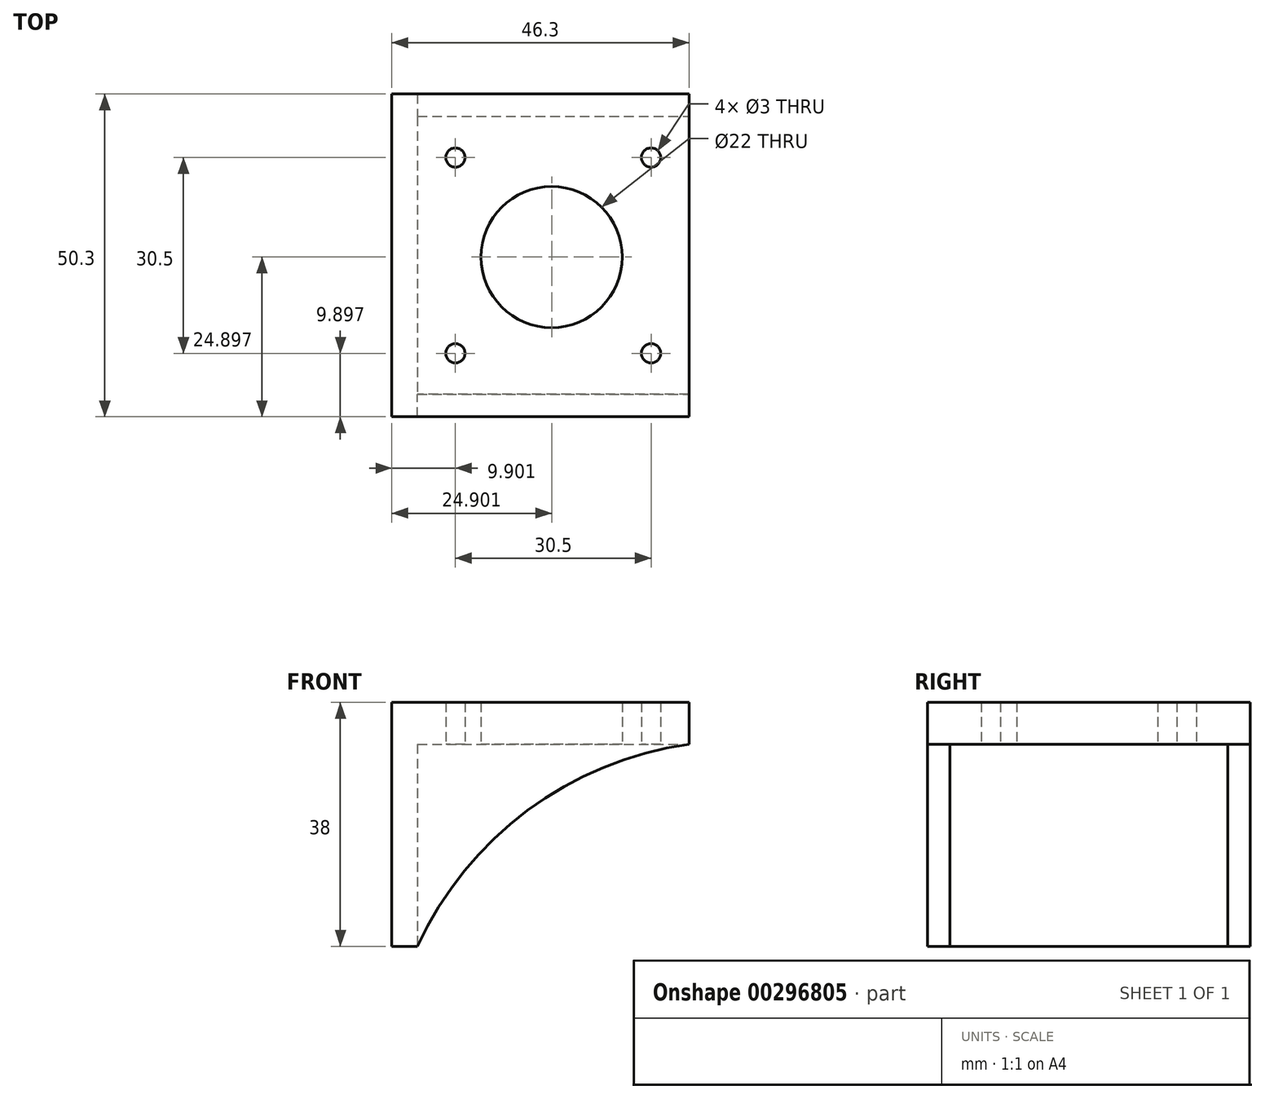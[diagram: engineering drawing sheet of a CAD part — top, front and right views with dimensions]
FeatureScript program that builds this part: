
annotation { "Feature Type Name" : "Feature", "Feature Type Description" : "" }
export const myFeature = defineFeature(function(context is Context, id is Id, definition is map)
    precondition{}
    {
        {
            var Q0;
            Q0=qCreatedBy(makeId("Top.planeOp"),FACE);
            var sketch = newSketch(context, id + "F0", { "sketchPlane" : qUnion([Q0])});
            skLineSegment(sketch, "E0.bottom", {"start": v(-20.2, 20.3) * mm, "end": v(22.1, 20.3) * mm});
            skLineSegment(sketch, "E0.top", {"start": v(-20.2, -22) * mm, "end": v(22.1, -22) * mm});
            skLineSegment(sketch, "E0.left", {"start": v(-20.2, 20.3) * mm, "end": v(-20.2, -22) * mm});
            skLineSegment(sketch, "E0.right", {"start": v(22.1, 20.3) * mm, "end": v(22.1, -22) * mm});
            skPoint(sketch, "E1", {"position": v(-14.3, 14.4) * mm});
            skPoint(sketch, "E2.0.1.0", {"position": v(-14.3, -16.1) * mm});
            skPoint(sketch, "E2.1.0.0", {"position": v(16.2, 14.4) * mm});
            skPoint(sketch, "E2.1.1.0", {"position": v(16.2, -16.1) * mm});
            skLineSegment(sketch, "E2.direction1", {"start": v(-14.3, 14.4) * mm, "end": v(16.2, 14.4) * mm, "construction": true});
            skLineSegment(sketch, "E2.direction2", {"start": v(-14.3, 14.4) * mm, "end": v(-14.3, -16.1) * mm, "construction": true});
            skCircle(sketch, "E3", {"center": v(-14.3, 14.4) * mm, "radius": 1.5 * mm});
            skCircle(sketch, "E4", {"center": v(16.2, 14.4) * mm, "radius": 1.5 * mm});
            skCircle(sketch, "E5", {"center": v(16.2, -16.1) * mm, "radius": 1.5 * mm});
            skCircle(sketch, "E6", {"center": v(-14.3, -16.1) * mm, "radius": 1.5 * mm});
            skCircle(sketch, "E7", {"center": v(0.7, -1.1) * mm, "radius": 2.5 * mm});
            skCircle(sketch, "E8", {"center": v(0.7, -1.1) * mm, "radius": 3.5 * mm, "construction": true});
            skCircle(sketch, "E9", {"center": v(0.7, -1.1) * mm, "radius": 11 * mm});
            skSolve(sketch);
        }
        {
            var Q0;
            Q0=makeQuery(id+"F0.imprint","IMPRINT",FACE,{"disambiguationData":[TD([[makeQuery(id+"F0.imprint","IMPRINT",EDGE,{"derivedFrom":sQuery(id+"F0.wireOp",EDGE,"E0.bottom")}),-1.0]])]});
            extrude(context, id + "F1", {"entities" : qUnion([Q0]), "depth" : 6.5 * mm});
        }
        {
            var Q0;
            Q0=makeQuery(id+"F1.opExtrude","SWEPT_FACE",FACE,{"disambiguationData":[OSD([sQuery(id+"F0.wireOp",EDGE,"E0.left")])]});
            var sketch = newSketch(context, id + "F2", { "sketchPlane" : qUnion([Q0])});
            skLineSegment(sketch, "E10.bottom", {"start": v(-20.3, 6.5) * mm, "end": v(22, 6.5) * mm});
            skLineSegment(sketch, "E10.top", {"start": v(-20.3, -31.5) * mm, "end": v(22, -31.5) * mm});
            skLineSegment(sketch, "E10.left", {"start": v(-20.3, 6.5) * mm, "end": v(-20.3, -31.5) * mm});
            skLineSegment(sketch, "E10.right", {"start": v(22, 6.5) * mm, "end": v(22, -31.5) * mm});
            skSolve(sketch);
        }
        {
            var Q0;
            Q0=qSketchRegion(id+"F2",true);
            extrude(context, id + "F3", {"entities" : qUnion([Q0]), "operationType" : NewBodyOperationType.ADD, "depth" : 4 * mm});
        }
        {
            var Q0;
            Q0=makeQuery(id+"F3.boolean.opBoolean","MERGE",FACE,{"derivedFrom":[makeQuery(id+"F1.opExtrude","SWEPT_FACE",FACE,{"disambiguationData":[OSD([sQuery(id+"F0.wireOp",EDGE,"E0.top")])]}),makeQuery(id+"F3.opExtrude","SWEPT_FACE",FACE,{"disambiguationData":[OSD([sQuery(id+"F2.wireOp",EDGE,"E10.right")])]})]});
            var sketch = newSketch(context, id + "F4", { "sketchPlane" : qUnion([Q0])});
            skArc(sketch, "E11", {"start": v(22.1, 0) * mm, "mid": v(-3.08, -10.35) * mm, "end": v(-20.2, -31.5) * mm});
            skSolve(sketch);
        }
        {
            var Q0;
            Q0=makeQuery(id+"F3.boolean.opBoolean","MERGE",FACE,{"derivedFrom":[makeQuery(id+"F1.opExtrude","SWEPT_FACE",FACE,{"disambiguationData":[OSD([sQuery(id+"F0.wireOp",EDGE,"E0.bottom")])]}),makeQuery(id+"F3.opExtrude","SWEPT_FACE",FACE,{"disambiguationData":[OSD([sQuery(id+"F2.wireOp",EDGE,"E10.left")])]})]});
            var sketch = newSketch(context, id + "F5", { "sketchPlane" : qUnion([Q0])});
            skArc(sketch, "E12", {"start": v(20.2, -31.5) * mm, "mid": v(3.08, -10.35) * mm, "end": v(-22.1, 0) * mm});
            skSolve(sketch);
        }
        {
            var Q0;
            Q0=makeQuery(id+"F5.imprint","IMPRINT",FACE,{"disambiguationData":[TD([[makeQuery(id+"F5.imprint","IMPRINT",EDGE,{"derivedFrom":sQuery(id+"F5.wireOp",EDGE,"E12")}),-1.0]])]});
            var Q1;
            {var subQ1=sQuery(id+"F0.wireOp",EDGE,"E0.bottom");Q1=makeQuery(id+"F5.imprint","IMPRINT",FACE,{"disambiguationData":[TD([[makeQuery(id+"F5.imprint","IMPRINT",EDGE,{"derivedFrom":makeQuery(id+"F1.opExtrude","CAP_EDGE",EDGE,{"disambiguationData":[OSD([subQ1])],"isStart":true})}),-1.0]])]});}
            extrude(context, id + "F6", {"entities" : qUnion([Q0, Q1]), "operationType" : NewBodyOperationType.ADD, "depth" : 4 * mm});
        }
        {
            var Q0;
            Q0=makeQuery(id+"F4.imprint","IMPRINT",FACE,{"disambiguationData":[TD([[makeQuery(id+"F4.imprint","IMPRINT",EDGE,{"derivedFrom":sQuery(id+"F4.wireOp",EDGE,"E11")}),-1.0]])]});
            var Q1;
            {var subQ1=sQuery(id+"F0.wireOp",EDGE,"E0.top");Q1=makeQuery(id+"F4.imprint","IMPRINT",FACE,{"disambiguationData":[TD([[makeQuery(id+"F4.imprint","IMPRINT",EDGE,{"derivedFrom":makeQuery(id+"F1.opExtrude","CAP_EDGE",EDGE,{"disambiguationData":[OSD([subQ1])],"isStart":true})}),1.0]])]});}
            extrude(context, id + "F7", {"entities" : qUnion([Q0, Q1]), "operationType" : NewBodyOperationType.ADD, "depth" : 4 * mm});
        }
        {
            var Q0;
            Q0=makeQuery(id+"F7.opExtrude","CAP_FACE",FACE,{"disambiguationData":[OSD([sQuery(id+"F0.wireOp",EDGE,"E0.top"),sQuery(id+"F0.wireOp",EDGE,"E0.right"),sQuery(id+"F2.wireOp",EDGE,"E10.bottom"),sQuery(id+"F2.wireOp",EDGE,"E10.top"),sQuery(id+"F2.wireOp",EDGE,"E10.right"),sQuery(id+"F4.wireOp",EDGE,"E11")])],"isStart":true});
            extrude(context, id + "F8", {"entities" : qUnion([Q0]), "operationType" : NewBodyOperationType.REMOVE, "oppositeDirection" : true, "depth" : 0.5 * mm});
        }
        {
            var Q0;
            Q0=makeQuery(id+"F6.opExtrude","CAP_FACE",FACE,{"disambiguationData":[OSD([sQuery(id+"F0.wireOp",EDGE,"E0.bottom"),sQuery(id+"F0.wireOp",EDGE,"E0.right"),sQuery(id+"F2.wireOp",EDGE,"E10.bottom"),sQuery(id+"F2.wireOp",EDGE,"E10.top"),sQuery(id+"F2.wireOp",EDGE,"E10.left"),sQuery(id+"F5.wireOp",EDGE,"E12")])],"isStart":true});
            extrude(context, id + "F9", {"entities" : qUnion([Q0]), "operationType" : NewBodyOperationType.REMOVE, "oppositeDirection" : true, "depth" : 0.5 * mm});
        }
    });
